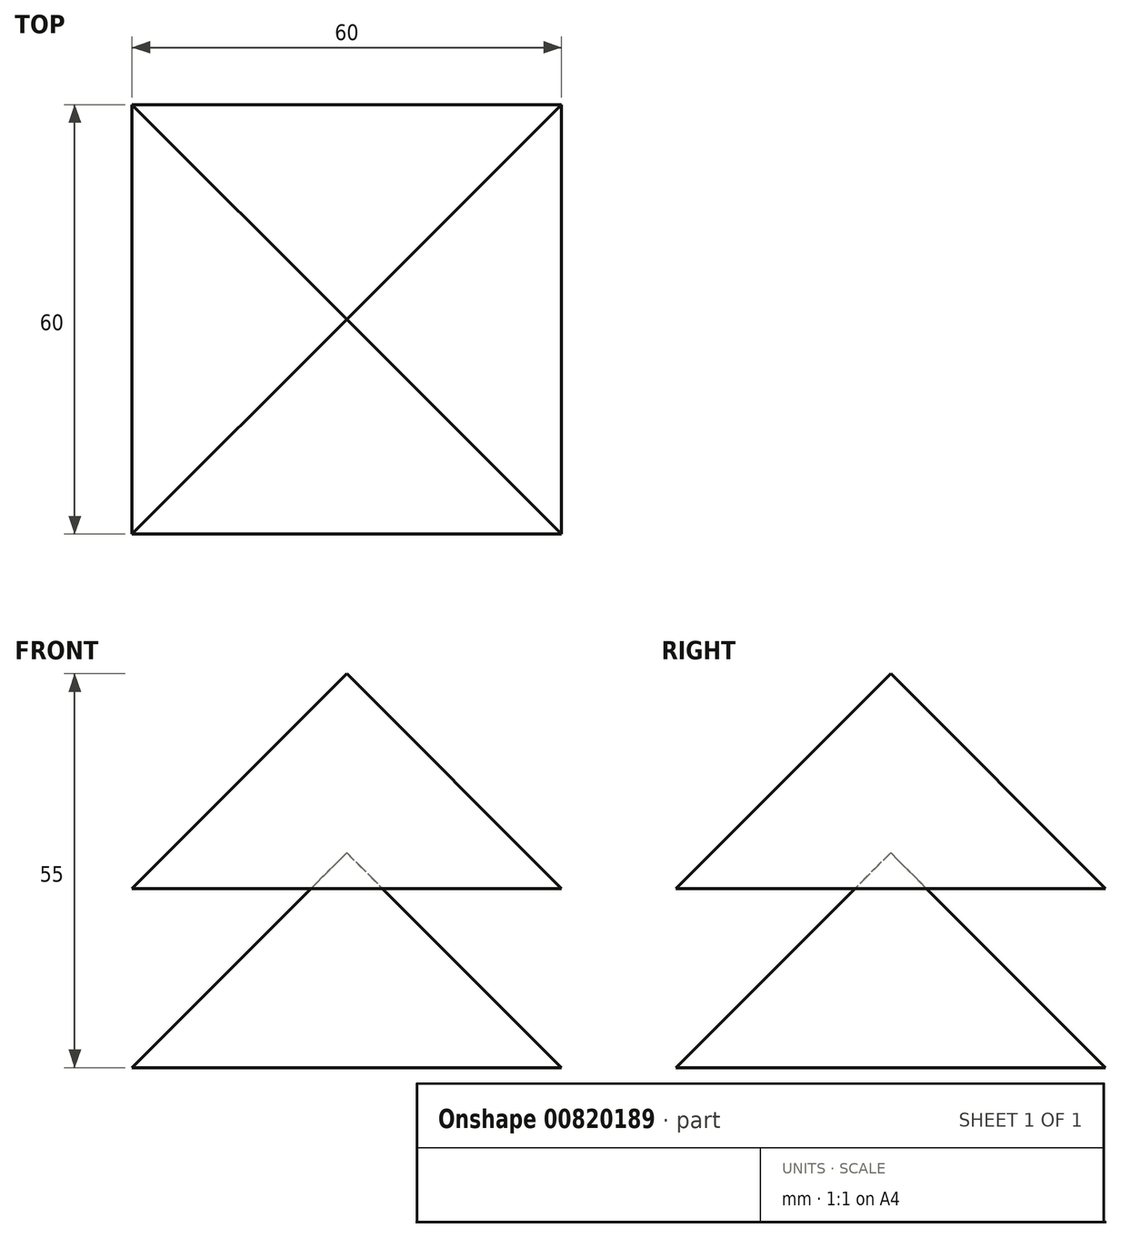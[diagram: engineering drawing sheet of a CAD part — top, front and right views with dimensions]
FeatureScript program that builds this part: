
annotation { "Feature Type Name" : "Feature", "Feature Type Description" : "" }
export const myFeature = defineFeature(function(context is Context, id is Id, definition is map)
    precondition{}
    {
        {
            var Q0;
            Q0=qCreatedBy(makeId("Top.planeOp"),FACE);
            var sketch = newSketch(context, id + "F0", { "sketchPlane" : qUnion([Q0])});
            skLineSegment(sketch, "E0.bottom", {"start": v(30, 30) * mm, "end": v(-30, 30) * mm});
            skLineSegment(sketch, "E0.top", {"start": v(30, -30) * mm, "end": v(-30, -30) * mm});
            skLineSegment(sketch, "E0.left", {"start": v(30, 30) * mm, "end": v(30, -30) * mm});
            skLineSegment(sketch, "E0.right", {"start": v(-30, 30) * mm, "end": v(-30, -30) * mm});
            skPoint(sketch, "E0.middle", {"position": v(0, 0) * mm});
            skSolve(sketch);
        }
        {
            var Q0;
            Q0=makeQuery(id+"F0.imprint","IMPRINT",FACE,{"disambiguationData":[TD([[makeQuery(id+"F0.imprint","IMPRINT",EDGE,{"derivedFrom":sQuery(id+"F0.wireOp",EDGE,"E0.bottom")}),1.0]])]});
            extrude(context, id + "F1", {"entities" : qUnion([Q0]), "depth" : 30 * mm, "offsetDistance" : 25.4 * mm, "hasDraft" : true, "draftAngle" : 45 * degree, "draftPullDirection" : true});
        }
        {
            var Q0;
            Q0=qCreatedBy(makeId("Top.planeOp"),FACE);
            var Q1;
            Q1 = qBodyType(qCreatedBy(id + "F3" ,EDGE), BodyType.WIRE);
            cPlane(context, id + "F2", {"entities" : qUnion([Q0, Q1]), "cplaneType" : CPlaneType.OFFSET, "offset" : 25 * mm, "oppositeDirection" : true, "width" : 152.4 * mm, "height" : 152.4 * mm});
        }
        {
            var Q0;
            Q0=qCreatedBy(id+"F2.planeOp",FACE);
            var sketch = newSketch(context, id + "F3", { "sketchPlane" : qUnion([Q0])});
            skLineSegment(sketch, "E1.bottom", {"start": v(-30, -30) * mm, "end": v(30, -30) * mm});
            skLineSegment(sketch, "E1.top", {"start": v(-30, 30) * mm, "end": v(30, 30) * mm});
            skLineSegment(sketch, "E1.left", {"start": v(-30, -30) * mm, "end": v(-30, 30) * mm});
            skLineSegment(sketch, "E1.right", {"start": v(30, -30) * mm, "end": v(30, 30) * mm});
            skPoint(sketch, "E1.middle", {"position": v(0, 0) * mm});
            skSolve(sketch);
        }
        {
            var Q0;
            Q0 = qSketchRegion(id + "F3", true);
            extrude(context, id + "F4", {"entities" : qUnion([Q0]), "depth" : 30 * mm, "offsetDistance" : 25.4 * mm, "hasDraft" : true, "draftAngle" : 45 * degree, "draftPullDirection" : true});
        }
    });
